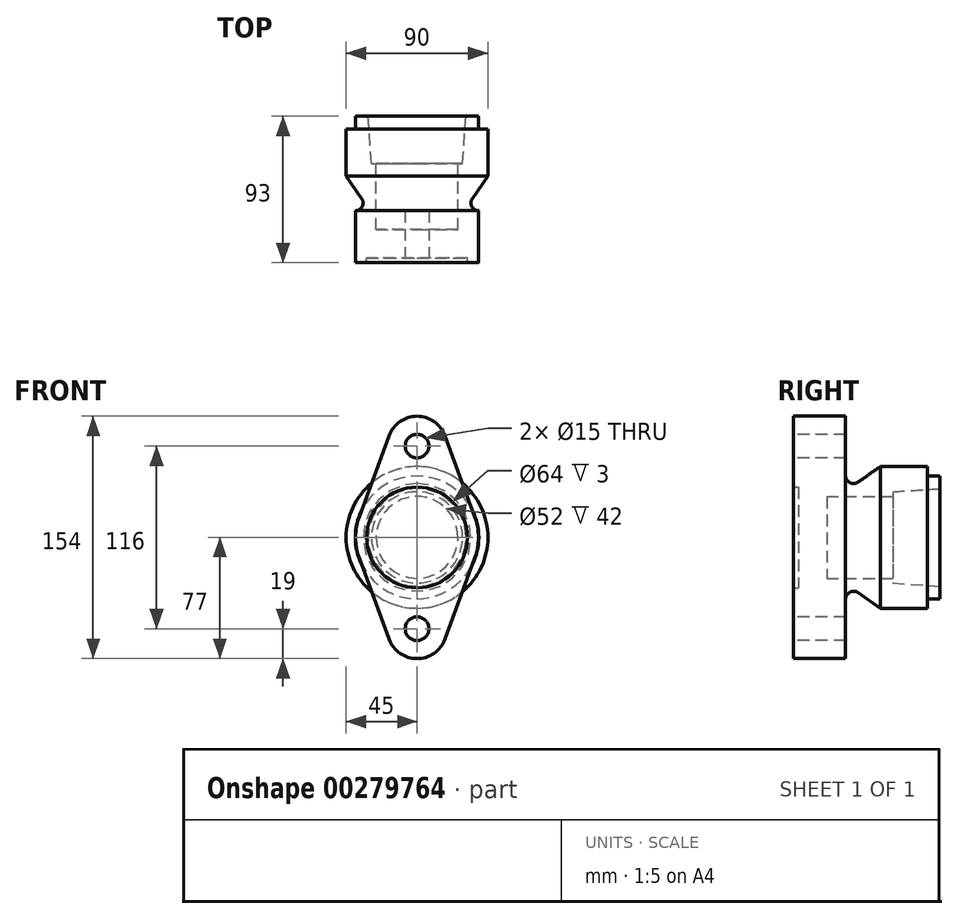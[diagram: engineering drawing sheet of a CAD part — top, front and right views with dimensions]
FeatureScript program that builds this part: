
annotation { "Feature Type Name" : "Feature", "Feature Type Description" : "" }
export const myFeature = defineFeature(function(context is Context, id is Id, definition is map)
    precondition{}
    {
        {
            var Q0;
            Q0=qCreatedBy(makeId("Right.planeOp"),FACE);
            var sketch = newSketch(context, id + "F0", { "sketchPlane" : qUnion([Q0])});
            skLineSegment(sketch, "E0", {"start": v(21, 0) * mm, "end": v(3, 0) * mm});
            skLineSegment(sketch, "E1", {"start": v(3, 0) * mm, "end": v(3, 32) * mm});
            skLineSegment(sketch, "E2", {"start": v(0, 32) * mm, "end": v(3, 32) * mm});
            skLineSegment(sketch, "E3", {"start": v(0, 32) * mm, "end": v(0, 39) * mm});
            skLineSegment(sketch, "E4", {"start": v(0, 39) * mm, "end": v(33, 39) * mm});
            skPoint(sketch, "E5.end.orphan", {"position": v(70.4, 0) * mm});
            skLineSegment(sketch, "E6", {"start": v(85, 45) * mm, "end": v(85, 39) * mm});
            skLineSegment(sketch, "E7", {"start": v(85, 39) * mm, "end": v(93, 39) * mm});
            skLineSegment(sketch, "E8", {"start": v(93, 39) * mm, "end": v(93, 31) * mm});
            skLineSegment(sketch, "E9", {"start": v(93, 31) * mm, "end": v(63, 29) * mm});
            skLineSegment(sketch, "E10", {"start": v(63, 29) * mm, "end": v(63, 26) * mm});
            skPoint(sketch, "E11.end.orphan", {"position": v(21, 26) * mm});
            skLineSegment(sketch, "E12", {"start": v(21, 0) * mm, "end": v(21, 26) * mm});
            skLineSegment(sketch, "E13", {"start": v(63, 26) * mm, "end": v(21, 26) * mm});
            skLineSegment(sketch, "E14", {"start": v(33, 39.2) * mm, "end": v(33, 39) * mm});
            skLineSegment(sketch, "E15", {"start": v(85, 45) * mm, "end": v(55, 45) * mm});
            skLineSegment(sketch, "E16", {"start": v(55, 45) * mm, "end": v(40.87, 35.1) * mm});
            skPoint(sketch, "E17.visualSharp", {"position": v(33, 29.6) * mm});
            skArc(sketch, "E17.filletArc", {"start": v(33, 39.2) * mm, "mid": v(35.7, 34.77) * mm, "end": v(40.87, 35.1) * mm});
            skSolve(sketch);
        }
        {
            var Q0;
            Q0=makeQuery(id+"F0.imprint","IMPRINT",FACE,{"disambiguationData":[TD([[makeQuery(id+"F0.imprint","IMPRINT",EDGE,{"derivedFrom":sQuery(id+"F0.wireOp",EDGE,"E0")}),-1.0]])]});
            var Q1;
            Q1=sQuery(id+"F0.wireOp",EDGE,"E0");
            revolve(context, id + "F1", {"entities" : qUnion([Q0]), "axis" : qUnion([Q1]), "revolveType" : RevolveType.FULL});
        }
        {
            var Q0;
            Q0=qCreatedBy(makeId("Front.planeOp"),FACE);
            var sketch = newSketch(context, id + "F2", { "sketchPlane" : qUnion([Q0])});
            skLineSegment(sketch, "E18", {"start": v(0, -3.24) * mm, "end": v(0, 122.41) * mm});
            skLineSegment(sketch, "E19", {"start": v(-49.12, 58) * mm, "end": v(51.78, 58) * mm});
            skCircle(sketch, "E20", {"center": v(0, 58) * mm, "radius": 7.5 * mm});
            skArc(sketch, "E21", {"start": v(17.83, 64.55) * mm, "mid": v(0, 77) * mm, "end": v(-17.83, 64.55) * mm});
            skPoint(sketch, "E22.end.orphan", {"position": v(20.24, 58) * mm});
            skLineSegment(sketch, "E23", {"start": v(-17.83, 64.55) * mm, "end": v(-37.42, 11.24) * mm});
            skLineSegment(sketch, "E24", {"start": v(17.83, 64.55) * mm, "end": v(20.24, 58) * mm});
            skLineSegment(sketch, "E25", {"start": v(17.83, 64.55) * mm, "end": v(37.42, 11.24) * mm});
            skArc(sketch, "E26", {"start": v(-36.6, -13.45) * mm, "mid": v(0, -39) * mm, "end": v(36.6, -13.45) * mm});
            skLineSegment(sketch, "E27", {"start": v(-65.65, 0) * mm, "end": v(70.93, 0) * mm, "construction": true});
            skLineSegment(sketch, "E28.MirrorCS", {"start": v(17.83, -64.55) * mm, "end": v(37.42, -11.24) * mm});
            skArc(sketch, "E29.MirrorCS", {"start": v(17.83, -64.55) * mm, "mid": v(0, -77) * mm, "end": v(-17.83, -64.55) * mm});
            skLineSegment(sketch, "E30.MirrorCS", {"start": v(-17.83, -64.55) * mm, "end": v(-37.42, -11.24) * mm});
            skCircle(sketch, "E31.MirrorC", {"center": v(0, -58) * mm, "radius": 7.5 * mm});
            skArc(sketch, "E32.trimOffspring", {"start": v(36.6, 13.45) * mm, "mid": v(0, 39) * mm, "end": v(-36.6, 13.45) * mm});
            skSolve(sketch);
        }
        {
            var Q0;
            {var subQ1=sQuery(id+"F2.wireOp",EDGE,"E18");var subQ5=sQuery(id+"F2.wireOp",EDGE,"E32.trimOffspring");var subQ6=makeQuery(id+"F2.imprint","INTERSECT",VERTEX,{"derivedFrom":[subQ1,subQ5]});Q0=makeQuery(id+"F2.imprint","IMPRINT",FACE,{"disambiguationData":[TD([[makeQuery(id+"F2.imprint","IMPRINT",EDGE,{"disambiguationData":[TD([[subQ6,-1.0]])],"derivedFrom":subQ1}),-1.0]])]});}
            var Q1;
            {var subQ1=sQuery(id+"F2.wireOp",EDGE,"E21");var subQ3=sQuery(id+"F2.wireOp",EDGE,"E18");var subQ4=makeQuery(id+"F2.imprint","INTERSECT",VERTEX,{"derivedFrom":[subQ3,subQ1]});Q1=makeQuery(id+"F2.imprint","IMPRINT",FACE,{"disambiguationData":[TD([[makeQuery(id+"F2.imprint","IMPRINT",EDGE,{"disambiguationData":[TD([[subQ4,1.0]])],"derivedFrom":subQ3}),-1.0]])]});}
            var Q2;
            {var subQ1=sQuery(id+"F2.wireOp",EDGE,"E18");var subQ7=sQuery(id+"F2.wireOp",EDGE,"E21");var subQ9=makeQuery(id+"F2.imprint","INTERSECT",VERTEX,{"derivedFrom":[subQ1,subQ7]});Q2=makeQuery(id+"F2.imprint","IMPRINT",FACE,{"disambiguationData":[TD([[makeQuery(id+"F2.imprint","IMPRINT",EDGE,{"disambiguationData":[TD([[subQ9,1.0]])],"derivedFrom":subQ1}),1.0]])]});}
            var Q3;
            {var subQ5=sQuery(id+"F2.wireOp",EDGE,"E32.trimOffspring");var subQ7=sQuery(id+"F2.wireOp",EDGE,"E18");var subQ9=makeQuery(id+"F2.imprint","INTERSECT",VERTEX,{"derivedFrom":[subQ7,subQ5]});Q3=makeQuery(id+"F2.imprint","IMPRINT",FACE,{"disambiguationData":[TD([[makeQuery(id+"F2.imprint","IMPRINT",EDGE,{"disambiguationData":[TD([[subQ9,-1.0]])],"derivedFrom":subQ7}),1.0]])]});}
            var Q4;
            {var subQ1=sQuery(id+"F2.wireOp",EDGE,"E26");Q4=makeQuery(id+"F2.imprint","IMPRINT",FACE,{"disambiguationData":[TD([[makeQuery(id+"F2.imprint","IMPRINT",EDGE,{"derivedFrom":subQ1}),-1.0]])]});}
            extrude(context, id + "F3", {"entities" : qUnion([Q0, Q1, Q2, Q3, Q4]), "operationType" : NewBodyOperationType.ADD, "oppositeDirection" : true, "depth" : 33 * mm});
        }
    });
